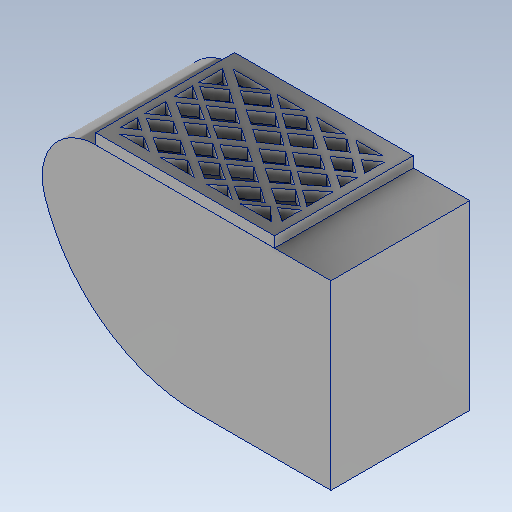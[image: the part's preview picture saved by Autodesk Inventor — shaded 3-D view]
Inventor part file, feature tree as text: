
AUTODESK INVENTOR PART (.ipt)
format: ipt  version: 2025.2 (Build 292293000, 293)  size: 730,112 bytes
history: native  units: mm
features: extrude x3, sketch x3, fillet x2
ambient origin geometry x8: Origin, YZ Plane, XZ Plane, XY Plane, X Axis, Y Axis, Z Axis, Center Point
bodies: Solid2 (feature_tree)
feature tree (8):
  extrude  "Extrusion2"  Depth=17.0mm
  fillet  "Fillet2"  Radius=17.0mm
  extrude  "Extrusion7"  Depth=1.0mm
  fillet  "Rundung3"  Radius=1.0mm
  extrude  "Extrusion8"  Depth=1.0mm
  sketch  "Sketch5"  dims[d56=13.0mm d57=0.0mm d67=15.6mm d97=17.0mm]
  sketch  "Sketch11"  dims[d98=15.0mm d99=1.0mm d100=1.0mm]
  sketch  "Skizze12"  dims[d101=1.0mm d102=1.0mm d103=0.0mm d104=0.0mm d105=5.0mm d106=27.5mm d107=1.0mm d108=0.0mm]
